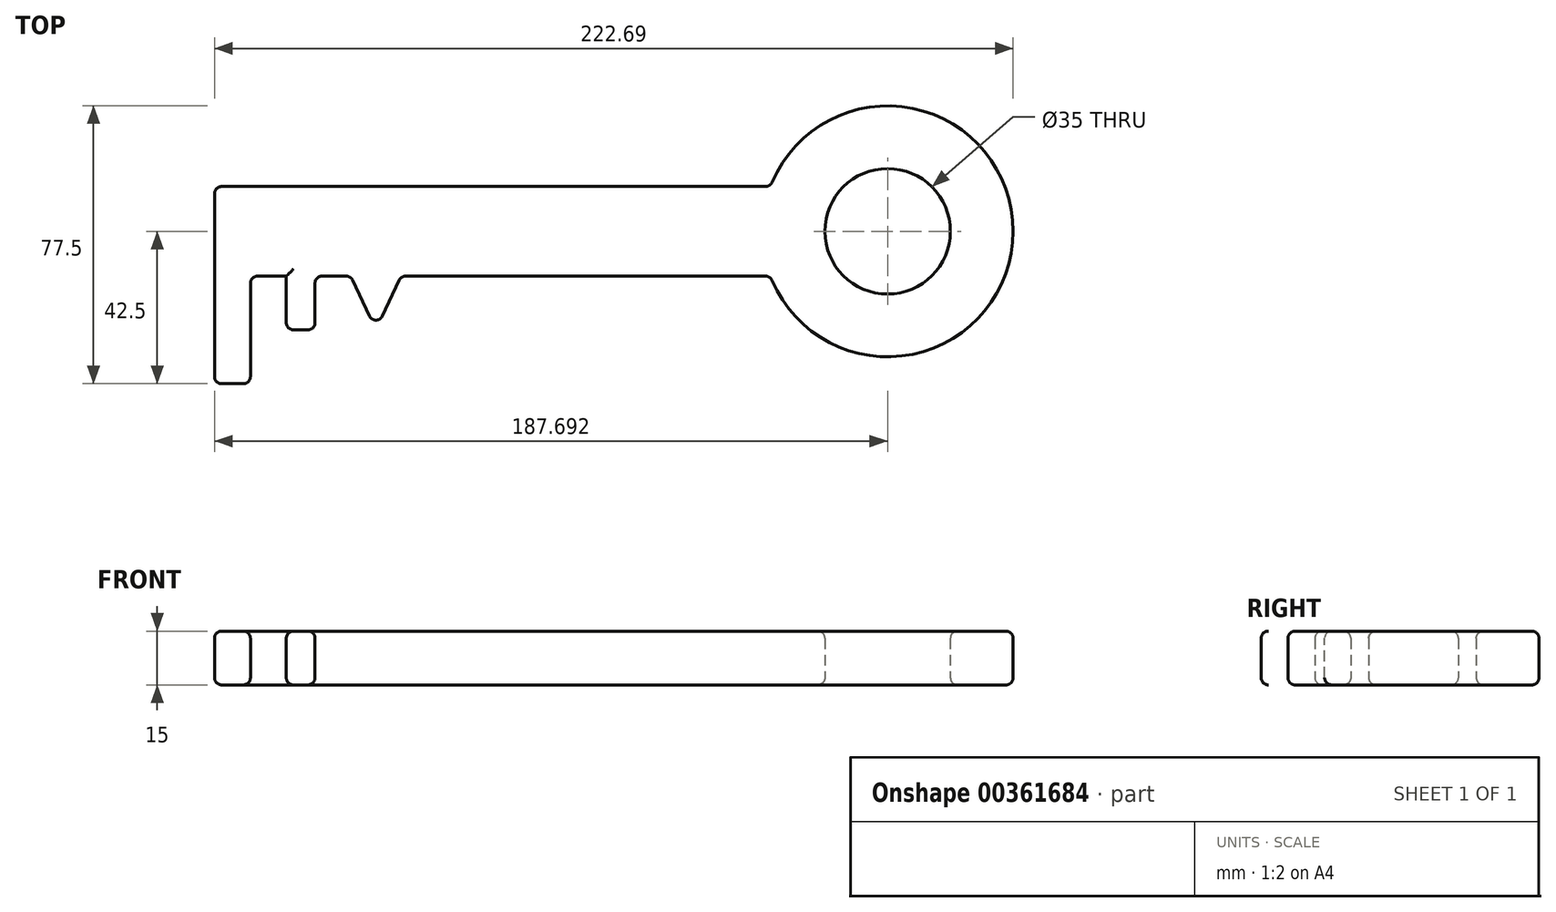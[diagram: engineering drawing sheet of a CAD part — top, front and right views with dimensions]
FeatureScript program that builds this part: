
annotation { "Feature Type Name" : "Feature", "Feature Type Description" : "" }
export const myFeature = defineFeature(function(context is Context, id is Id, definition is map)
    precondition{}
    {
        {
            var Q0;
            Q0=qCreatedBy(makeId("Top.planeOp"),FACE);
            var sketch = newSketch(context, id + "F0", { "sketchPlane" : qUnion([Q0])});
            skLineSegment(sketch, "E0.bottom", {"start": v(-73.25, 29.35) * mm, "end": v(81.75, 29.35) * mm});
            skLineSegment(sketch, "E0.top", {"start": v(-63.25, 4.35) * mm, "end": v(-53.25, 4.35) * mm});
            skLineSegment(sketch, "E0.left", {"start": v(-73.25, 29.35) * mm, "end": v(-73.25, 4.35) * mm});
            skLineSegment(sketch, "E1.top", {"start": v(-73.25, -25.65) * mm, "end": v(-63.25, -25.65) * mm});
            skLineSegment(sketch, "E1.left", {"start": v(-73.25, 4.35) * mm, "end": v(-73.25, -25.65) * mm});
            skLineSegment(sketch, "E1.right", {"start": v(-63.25, 4.35) * mm, "end": v(-63.25, -25.65) * mm});
            skLineSegment(sketch, "E2.top", {"start": v(-53.25, -10.65) * mm, "end": v(-45.25, -10.65) * mm});
            skLineSegment(sketch, "E2.left", {"start": v(-53.25, 4.35) * mm, "end": v(-53.25, -10.65) * mm});
            skLineSegment(sketch, "E2.right", {"start": v(-45.25, 4.35) * mm, "end": v(-45.25, -10.65) * mm});
            skLineSegment(sketch, "E3", {"start": v(-35.25, 4.35) * mm, "end": v(-28.25, -10.65) * mm});
            skLineSegment(sketch, "E4", {"start": v(-21.25, 4.35) * mm, "end": v(-28.25, -10.65) * mm});
            skArc(sketch, "E5", {"start": v(81.75, 4.35) * mm, "mid": v(149.44, 16.85) * mm, "end": v(81.75, 29.35) * mm});
            skCircle(sketch, "E6", {"center": v(114.44, 16.85) * mm, "radius": 17.5 * mm});
            skLineSegment(sketch, "E7", {"start": v(114.44, 16.85) * mm, "end": v(-73.25, 16.85) * mm, "construction": true});
            skLineSegment(sketch, "E8.trimOffspring", {"start": v(-21.25, 4.35) * mm, "end": v(81.75, 4.35) * mm});
            skLineSegment(sketch, "E9.trimOffspring", {"start": v(-45.25, 4.35) * mm, "end": v(-35.25, 4.35) * mm});
            skSolve(sketch);
        }
        {
            var Q0;
            Q0=makeQuery(id+"F0.imprint","IMPRINT",FACE,{"disambiguationData":[TD([[makeQuery(id+"F0.imprint","IMPRINT",EDGE,{"derivedFrom":sQuery(id+"F0.wireOp",EDGE,"E0.bottom")}),-1.0]])]});
            extrude(context, id + "F1", {"entities" : qUnion([Q0]), "depth" : 15 * mm});
        }
        {
            var Q0;
            Q0=makeQuery(id+"F1.opExtrude","CAP_EDGE",EDGE,{"disambiguationData":[OSD([sQuery(id+"F0.wireOp",EDGE,"E0.bottom")])],"isStart":false});
            var Q1;
            Q1=makeQuery(id+"F1.opExtrude","CAP_EDGE",EDGE,{"disambiguationData":[OSD([sQuery(id+"F0.wireOp",EDGE,"E0.left"),sQuery(id+"F0.wireOp",EDGE,"E1.left")])],"isStart":false});
            var Q2;
            Q2=makeQuery(id+"F1.opExtrude","CAP_EDGE",EDGE,{"disambiguationData":[OSD([sQuery(id+"F0.wireOp",EDGE,"E1.right")])],"isStart":false});
            var Q3;
            Q3=makeQuery(id+"F1.opExtrude","CAP_EDGE",EDGE,{"disambiguationData":[OSD([sQuery(id+"F0.wireOp",EDGE,"E1.top")])],"isStart":false});
            var Q4;
            Q4=makeQuery(id+"F1.opExtrude","CAP_EDGE",EDGE,{"disambiguationData":[OSD([sQuery(id+"F0.wireOp",EDGE,"E0.top")])],"isStart":false});
            var Q5;
            Q5=makeQuery(id+"F1.opExtrude","CAP_EDGE",EDGE,{"disambiguationData":[OSD([sQuery(id+"F0.wireOp",EDGE,"E2.left")])],"isStart":false});
            var Q6;
            Q6=makeQuery(id+"F1.opExtrude","CAP_EDGE",EDGE,{"disambiguationData":[OSD([sQuery(id+"F0.wireOp",EDGE,"E2.right")])],"isStart":false});
            var Q7;
            Q7=makeQuery(id+"F1.opExtrude","CAP_EDGE",EDGE,{"disambiguationData":[OSD([sQuery(id+"F0.wireOp",EDGE,"E2.top")])],"isStart":false});
            var Q8;
            Q8=makeQuery(id+"F1.opExtrude","CAP_EDGE",EDGE,{"disambiguationData":[OSD([sQuery(id+"F0.wireOp",EDGE,"E9.trimOffspring")])],"isStart":false});
            var Q9;
            Q9=makeQuery(id+"F1.opExtrude","CAP_EDGE",EDGE,{"disambiguationData":[OSD([sQuery(id+"F0.wireOp",EDGE,"E8.trimOffspring")])],"isStart":false});
            var Q10;
            Q10=makeQuery(id+"F1.opExtrude","CAP_EDGE",EDGE,{"disambiguationData":[OSD([sQuery(id+"F0.wireOp",EDGE,"E5")])],"isStart":false});
            var Q11;
            Q11=makeQuery(id+"F1.opExtrude","CAP_EDGE",EDGE,{"disambiguationData":[OSD([sQuery(id+"F0.wireOp",EDGE,"E6")])],"isStart":false});
            var Q12;
            Q12=makeQuery(id+"F1.opExtrude","SWEPT_FACE",FACE,{"disambiguationData":[OSD([sQuery(id+"F0.wireOp",EDGE,"E0.bottom")])]});
            var Q13;
            Q13=makeQuery(id+"F1.opExtrude","CAP_EDGE",EDGE,{"disambiguationData":[OSD([sQuery(id+"F0.wireOp",EDGE,"E5")])],"isStart":true});
            var Q14;
            Q14=makeQuery(id+"F1.opExtrude","SWEPT_FACE",FACE,{"disambiguationData":[OSD([sQuery(id+"F0.wireOp",EDGE,"E3")])]});
            var Q15;
            Q15=makeQuery(id+"F1.opExtrude","SWEPT_EDGE",EDGE,{"disambiguationData":[OSD([sQuery(id+"F0.wireOp",EDGE,"E4"),sQuery(id+"F0.wireOp",EDGE,"E8.trimOffspring")])]});
            var Q16;
            Q16=makeQuery(id+"F1.opExtrude","SWEPT_EDGE",EDGE,{"disambiguationData":[OSD([sQuery(id+"F0.wireOp",EDGE,"E3"),sQuery(id+"F0.wireOp",EDGE,"E4")])]});
            var Q17;
            Q17=makeQuery(id+"F1.opExtrude","SWEPT_EDGE",EDGE,{"disambiguationData":[OSD([sQuery(id+"F0.wireOp",EDGE,"E1.top"),sQuery(id+"F0.wireOp",EDGE,"E1.right")])]});
            var Q18;
            Q18=makeQuery(id+"F1.opExtrude","SWEPT_EDGE",EDGE,{"disambiguationData":[OSD([sQuery(id+"F0.wireOp",EDGE,"E2.top"),sQuery(id+"F0.wireOp",EDGE,"E2.left")])]});
            var Q19;
            Q19=makeQuery(id+"F1.opExtrude","SWEPT_EDGE",EDGE,{"disambiguationData":[OSD([sQuery(id+"F0.wireOp",EDGE,"E1.top"),sQuery(id+"F0.wireOp",EDGE,"E1.left")])]});
            var Q20;
            Q20=makeQuery(id+"F1.opExtrude","SWEPT_EDGE",EDGE,{"disambiguationData":[OSD([sQuery(id+"F0.wireOp",EDGE,"E3"),sQuery(id+"F0.wireOp",EDGE,"E9.trimOffspring")])]});
            var Q21;
            Q21=makeQuery(id+"F1.opExtrude","SWEPT_EDGE",EDGE,{"disambiguationData":[OSD([sQuery(id+"F0.wireOp",EDGE,"E5"),sQuery(id+"F0.wireOp",EDGE,"E8.trimOffspring")])]});
            var Q22;
            Q22=makeQuery(id+"F1.opExtrude","SWEPT_FACE",FACE,{"disambiguationData":[OSD([sQuery(id+"F0.wireOp",EDGE,"E5")])]});
            var Q23;
            Q23=makeQuery(id+"F1.opExtrude","CAP_EDGE",EDGE,{"disambiguationData":[OSD([sQuery(id+"F0.wireOp",EDGE,"E8.trimOffspring")])],"isStart":true});
            var Q24;
            Q24=makeQuery(id+"F1.opExtrude","CAP_EDGE",EDGE,{"disambiguationData":[OSD([sQuery(id+"F0.wireOp",EDGE,"E6")])],"isStart":true});
            var Q25;
            Q25=makeQuery(id+"F1.opExtrude","CAP_EDGE",EDGE,{"disambiguationData":[OSD([sQuery(id+"F0.wireOp",EDGE,"E1.top")])],"isStart":true});
            var Q26;
            Q26=makeQuery(id+"F1.opExtrude","CAP_EDGE",EDGE,{"disambiguationData":[OSD([sQuery(id+"F0.wireOp",EDGE,"E2.top")])],"isStart":true});
            var Q27;
            Q27=makeQuery(id+"F1.opExtrude","CAP_EDGE",EDGE,{"disambiguationData":[OSD([sQuery(id+"F0.wireOp",EDGE,"E4")])],"isStart":true});
            var Q28;
            Q28=makeQuery(id+"F1.opExtrude","SWEPT_EDGE",EDGE,{"disambiguationData":[OSD([sQuery(id+"F0.wireOp",EDGE,"E0.bottom"),sQuery(id+"F0.wireOp",EDGE,"E0.left")])]});
            var Q29;
            Q29=makeQuery(id+"F1.opExtrude","SWEPT_FACE",FACE,{"disambiguationData":[OSD([sQuery(id+"F0.wireOp",EDGE,"E0.left"),sQuery(id+"F0.wireOp",EDGE,"E1.left")])]});
            var Q30;
            Q30=makeQuery(id+"F1.opExtrude","SWEPT_FACE",FACE,{"disambiguationData":[OSD([sQuery(id+"F0.wireOp",EDGE,"E6")])]});
            var Q31;
            Q31=makeQuery(id+"F1.opExtrude","CAP_EDGE",EDGE,{"disambiguationData":[OSD([sQuery(id+"F0.wireOp",EDGE,"E0.bottom")])],"isStart":true});
            var Q32;
            Q32=makeQuery(id+"F1.opExtrude","CAP_FACE",FACE,{"disambiguationData":[OSD([sQuery(id+"F0.wireOp",EDGE,"E0.bottom"),sQuery(id+"F0.wireOp",EDGE,"E0.top"),sQuery(id+"F0.wireOp",EDGE,"E0.left"),sQuery(id+"F0.wireOp",EDGE,"E1.top"),sQuery(id+"F0.wireOp",EDGE,"E1.left"),sQuery(id+"F0.wireOp",EDGE,"E1.right"),sQuery(id+"F0.wireOp",EDGE,"E2.top"),sQuery(id+"F0.wireOp",EDGE,"E2.left"),sQuery(id+"F0.wireOp",EDGE,"E2.right"),sQuery(id+"F0.wireOp",EDGE,"E3"),sQuery(id+"F0.wireOp",EDGE,"E4"),sQuery(id+"F0.wireOp",EDGE,"E5"),sQuery(id+"F0.wireOp",EDGE,"E6"),sQuery(id+"F0.wireOp",EDGE,"E8.trimOffspring"),sQuery(id+"F0.wireOp",EDGE,"E9.trimOffspring")])],"isStart":false});
            var Q33;
            Q33=makeQuery(id+"F1.opExtrude","CAP_EDGE",EDGE,{"disambiguationData":[OSD([sQuery(id+"F0.wireOp",EDGE,"E1.right")])],"isStart":true});
            var Q34;
            Q34=makeQuery(id+"F1.opExtrude","CAP_EDGE",EDGE,{"disambiguationData":[OSD([sQuery(id+"F0.wireOp",EDGE,"E9.trimOffspring")])],"isStart":true});
            var Q35;
            Q35=makeQuery(id+"F1.opExtrude","CAP_EDGE",EDGE,{"disambiguationData":[OSD([sQuery(id+"F0.wireOp",EDGE,"E2.left")])],"isStart":true});
            var Q36;
            Q36=makeQuery(id+"F1.opExtrude","CAP_EDGE",EDGE,{"disambiguationData":[OSD([sQuery(id+"F0.wireOp",EDGE,"E2.right")])],"isStart":true});
            var Q37;
            Q37=makeQuery(id+"F1.opExtrude","CAP_EDGE",EDGE,{"disambiguationData":[OSD([sQuery(id+"F0.wireOp",EDGE,"E0.top")])],"isStart":true});
            var Q38;
            Q38=makeQuery(id+"F1.opExtrude","SWEPT_EDGE",EDGE,{"disambiguationData":[OSD([sQuery(id+"F0.wireOp",EDGE,"E2.top"),sQuery(id+"F0.wireOp",EDGE,"E2.right")])]});
            var Q39;
            Q39=makeQuery(id+"F1.opExtrude","SWEPT_EDGE",EDGE,{"disambiguationData":[OSD([sQuery(id+"F0.wireOp",EDGE,"E2.right"),sQuery(id+"F0.wireOp",EDGE,"E9.trimOffspring")])]});
            var Q40;
            Q40=makeQuery(id+"F1.opExtrude","SWEPT_EDGE",EDGE,{"disambiguationData":[OSD([sQuery(id+"F0.wireOp",EDGE,"E0.top"),sQuery(id+"F0.wireOp",EDGE,"E1.right")])]});
            var Q41;
            Q41=makeQuery(id+"F1.opExtrude","CAP_EDGE",EDGE,{"disambiguationData":[OSD([sQuery(id+"F0.wireOp",EDGE,"E3")])],"isStart":true});
            var Q42;
            Q42=makeQuery(id+"F1.opExtrude","CAP_EDGE",EDGE,{"disambiguationData":[OSD([sQuery(id+"F0.wireOp",EDGE,"E3")])],"isStart":false});
            fillet(context, id + "F2", {"entities" : qUnion([Q0, Q1, Q2, Q3, Q4, Q5, Q6, Q7, Q8, Q9, Q10, Q11, Q12, Q13, Q14, Q15, Q16, Q17, Q18, Q19, Q20, Q21, Q22, Q23, Q24, Q25, Q26, Q27, Q28, Q29, Q30, Q31, Q32, Q33, Q34, Q35, Q36, Q37, Q38, Q39, Q40, Q41, Q42]), "radius" : 2 * mm, "tangentPropagation" : true, "allowEdgeOverflow" : false});
        }
    });
